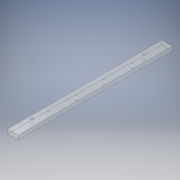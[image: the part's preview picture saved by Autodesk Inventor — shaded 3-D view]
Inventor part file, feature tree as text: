
AUTODESK INVENTOR PART (.ipt)
format: ipt  version: 2019 (Build 230136000, 136)  size: 126,464 bytes
history: native  units: mm
features: extrude x1, sketch x1
ambient origin geometry x8: Origin, YZ Plane, XZ Plane, XY Plane, X Axis, Y Axis, Z Axis, Center Point
bodies: Body1 (feature_tree)
feature tree (2):
  extrude  "Extrusion2"  Depth=15.0mm
  sketch  "Sketch2"  dims[d31=6.0mm d32=0.0mm d76=15.0mm d78=30.0mm d80=5.0mm d81=4.5mm d82=30.0mm d83=220.0mm d84=1.9mm d85=7.5mm d86=20.0mm d87=40.0mm d89=40.0mm d90=10.0mm d92=10.0mm]
